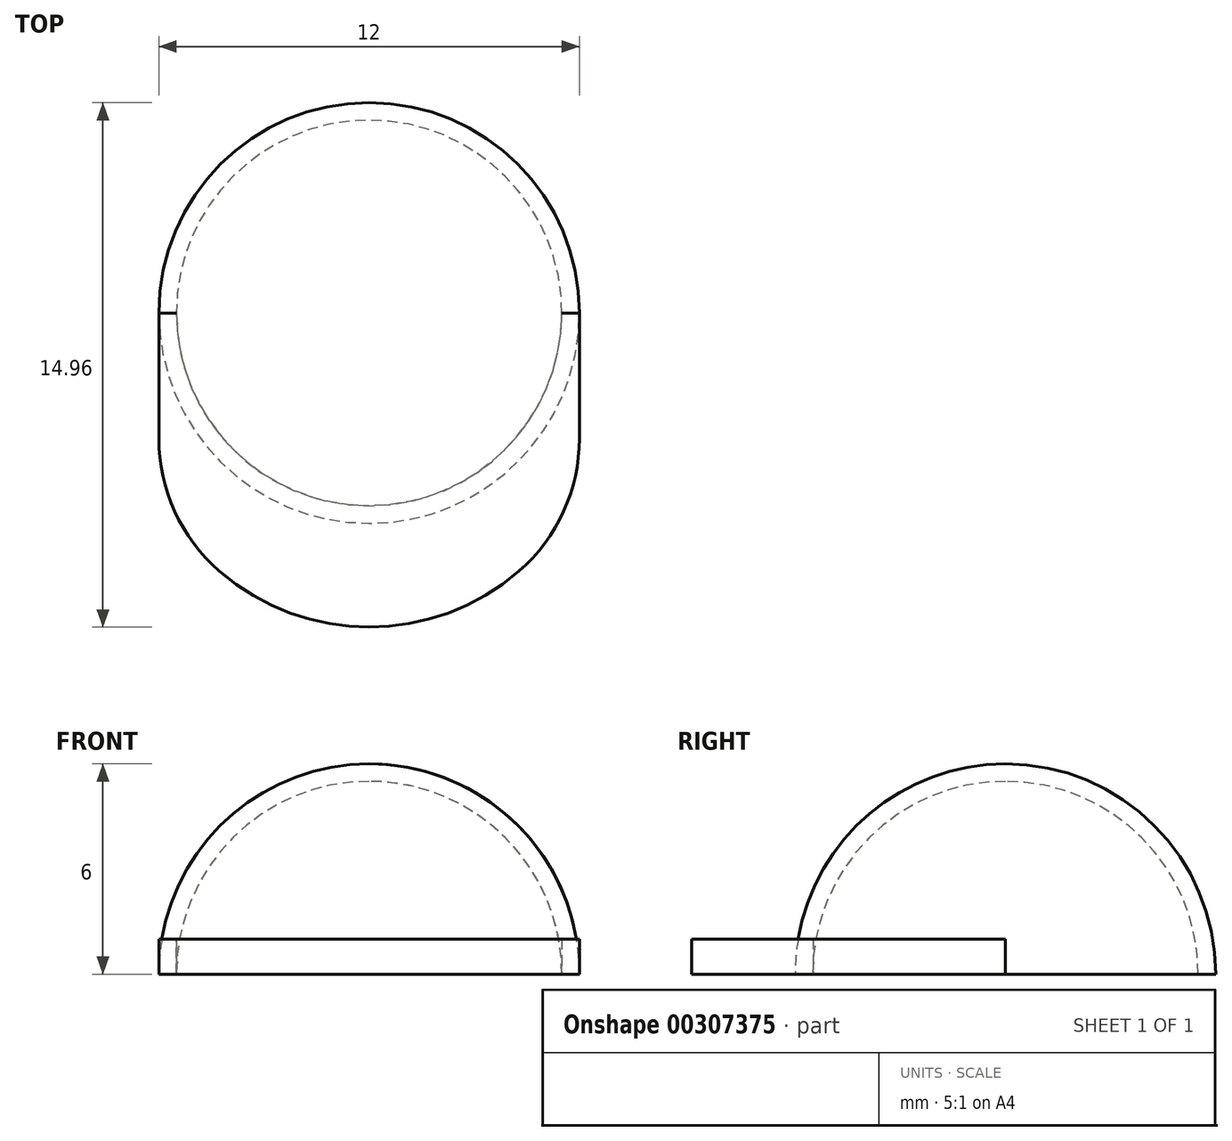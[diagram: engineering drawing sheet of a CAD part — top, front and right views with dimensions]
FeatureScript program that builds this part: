
annotation { "Feature Type Name" : "Feature", "Feature Type Description" : "" }
export const myFeature = defineFeature(function(context is Context, id is Id, definition is map)
    precondition{}
    {
        {
            var Q0;
            Q0=qCreatedBy(makeId("Front.planeOp"),FACE);
            var sketch = newSketch(context, id + "F0", { "sketchPlane" : qUnion([Q0])});
            skArc(sketch, "E0", {"start": v(6, 0) * mm, "mid": v(4.24, 4.24) * mm, "end": v(0, 6) * mm});
            skLineSegment(sketch, "E1", {"start": v(0, 6) * mm, "end": v(0, 0) * mm});
            skLineSegment(sketch, "E2", {"start": v(0, 0) * mm, "end": v(6, 0) * mm});
            skArc(sketch, "E3", {"start": v(5.5, 0) * mm, "mid": v(3.89, 3.89) * mm, "end": v(0, 5.5) * mm});
            skLineSegment(sketch, "E4", {"start": v(0, 5.5) * mm, "end": v(0, 2.5) * mm, "construction": true});
            skLineSegment(sketch, "E5", {"start": v(0, 2.5) * mm, "end": v(4.9, 2.5) * mm, "construction": true});
            skLineSegment(sketch, "E6", {"start": v(0, 2.5) * mm, "end": v(3.5, 2.5) * mm, "construction": true});
            skLineSegment(sketch, "E7", {"start": v(3.5, 2.5) * mm, "end": v(3.5, 4.24) * mm});
            skLineSegment(sketch, "E8", {"start": v(3.5, 4.24) * mm, "end": v(3.5, 2.5) * mm});
            skLineSegment(sketch, "E9", {"start": v(2.5, 2.5) * mm, "end": v(3.5, 2.5) * mm});
            skLineSegment(sketch, "E10", {"start": v(2.5, 2.5) * mm, "end": v(2.5, 4.9) * mm});
            skSolve(sketch);
        }
        {
            var Q0;
            {var subQ0=sQuery(id+"F0.wireOp",EDGE,"E0");Q0=makeQuery(id+"F0.imprint","IMPRINT",FACE,{"disambiguationData":[TD([[makeQuery(id+"F0.imprint","IMPRINT",EDGE,{"derivedFrom":subQ0}),1.0]])]});}
            var Q1;
            {var subQ0=sQuery(id+"F0.wireOp",EDGE,"E8");Q1=makeQuery(id+"F0.imprint","IMPRINT",FACE,{"disambiguationData":[TD([[makeQuery(id+"F0.imprint","IMPRINT",EDGE,{"derivedFrom":subQ0}),-1.0]])]});}
            var Q2;
            Q2=sQuery(id+"F0.wireOp",EDGE,"E1");
            revolve(context, id + "F1", {"entities" : qUnion([Q0, Q1]), "axis" : qUnion([Q2]), "revolveType" : RevolveType.FULL});
        }
        {
            var Q0;
            Q0=makeQuery(id+"F1.opRevolve","SWEPT_FACE",FACE,{"disambiguationData":[OSD([sQuery(id+"F0.wireOp",EDGE,"E2")])]});
            var sketch = newSketch(context, id + "F2", { "sketchPlane" : qUnion([Q0])});
            skLineSegment(sketch, "E11.MirrorCS", {"start": v(6, 0) * mm, "end": v(6, 5) * mm, "construction": true});
            skLineSegment(sketch, "E12", {"start": v(-6, 0) * mm, "end": v(-6, 5) * mm, "construction": true});
            skLineSegment(sketch, "E13", {"start": v(-6, 0) * mm, "end": v(-6, 5) * mm});
            skLineSegment(sketch, "E14", {"start": v(6, 0) * mm, "end": v(6, 5) * mm});
            skArc(sketch, "E15", {"start": v(6, 5) * mm, "mid": v(0, 8.96) * mm, "end": v(-6, 5) * mm});
            skLineSegment(sketch, "E16", {"start": v(-6, 0) * mm, "end": v(-5.5, 0) * mm});
            skPoint(sketch, "E17.orphan", {"position": v(6, 10) * mm});
            skPoint(sketch, "E18.orphan", {"position": v(-6, 10) * mm});
            skLineSegment(sketch, "E19", {"start": v(5.5, 0) * mm, "end": v(6, 0) * mm});
            skArc(sketch, "E20", {"start": v(5.5, 0) * mm, "mid": v(0, 5.49) * mm, "end": v(-5.5, 0) * mm});
            skSolve(sketch);
        }
        {
            var Q0;
            Q0 = qSketchRegion(id + "F2", true);
            extrude(context, id + "F3", {"entities" : qUnion([Q0]), "oppositeDirection" : true, "depth" : 1 * mm, "offsetDistance" : 25 * mm, "hasSecondDirectionDraft" : true, "secondDirectionDraftAngle" : 3 * degree});
        }
        {
            var Q0;
            Q0=makeQuery(id+"F3.opExtrude","SWEPT_EDGE",EDGE,{"disambiguationData":[OSD([sQuery(id+"F2.wireOp",EDGE,"E14"),sQuery(id+"F2.wireOp",EDGE,"E15")])]});
            var Q1;
            Q1=makeQuery(id+"F3.opExtrude","SWEPT_EDGE",EDGE,{"disambiguationData":[OSD([sQuery(id+"F2.wireOp",EDGE,"E13"),sQuery(id+"F2.wireOp",EDGE,"E15")])]});
            fillet(context, id + "F4", {"entities" : qUnion([Q0, Q1]), "radius" : 5 * mm, "tangentPropagation" : true, "allowEdgeOverflow" : false});
        }
    });
